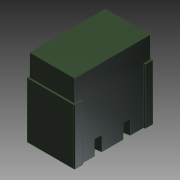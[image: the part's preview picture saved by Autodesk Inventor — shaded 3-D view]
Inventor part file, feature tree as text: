
AUTODESK INVENTOR PART (.ipt)
format: ipt  version: 2015 (Build 190159000, 159)  size: 166,912 bytes
history: native  units: in
note: dims shown in document units (in); Inventor stores cm internally (conversion verified against a paired STEP export)
features: other x21, extrude x5, sketch x5
ambient origin geometry x8: Origin, YZ Plane, XZ Plane, XY Plane, X Axis, Y Axis, Z Axis, Center Point
bodies: Solid1 (feature_tree)
feature tree (31):
  extrude  "Extrusion1"  Depth=0.141in TaperAngle=0.0deg
  extrude  "Extrusion2"  Depth=0.02in TaperAngle=0.0deg
  extrude  "Extrusion3"  [1 undecoded]
  extrude  "Extrusion4"  [1 undecoded]
  extrude  "Extrusion5"  [1 undecoded]
  other  "to_bm_terminals_XY"
  other  "to_bm_terminals_YZ"
  other  "to_bm_terminals_ZX"
  other  "to_bm_terminals_X"
  other  "to_bm_terminals_Y"
  other  "to_bm_terminals_Z"
  other  "to_bm_terminals_Center"
  other  "to_bodycover_XY"
  other  "to_bodycover_YZ"
  other  "to_bodycover_ZX"
  other  "to_bodycover_X"
  other  "to_bodycover_Y"
  other  "to_bodycover_Z"
  other  "to_bodycover_Center"
  other  "to_dummy_XY"
  other  "to_dummy_YZ"
  other  "to_dummy_ZX"
  other  "to_dummy_X"
  other  "to_dummy_Y"
  other  "to_dummy_Z"
  other  "to_dummy_Center"
  sketch  "Sketch_1"  dims[d0=0.361in d1=0.0in d2=0.141in d3=0.0in]
  sketch  "Sketch_2"  dims[d4=0.266in d5=0.0in d6=0.02in d7=0.0in]
  sketch  "Sketch_28"
  sketch  "Sketch_9"  dims[d8=0.02in d9=0.0in]
  sketch  "Sketch_10"
note: 3 required parameter values undecoded (feature->parameter linkage not recoverable at this tier; creation-order binding heuristic only, values carry confidence <= 0.55)
